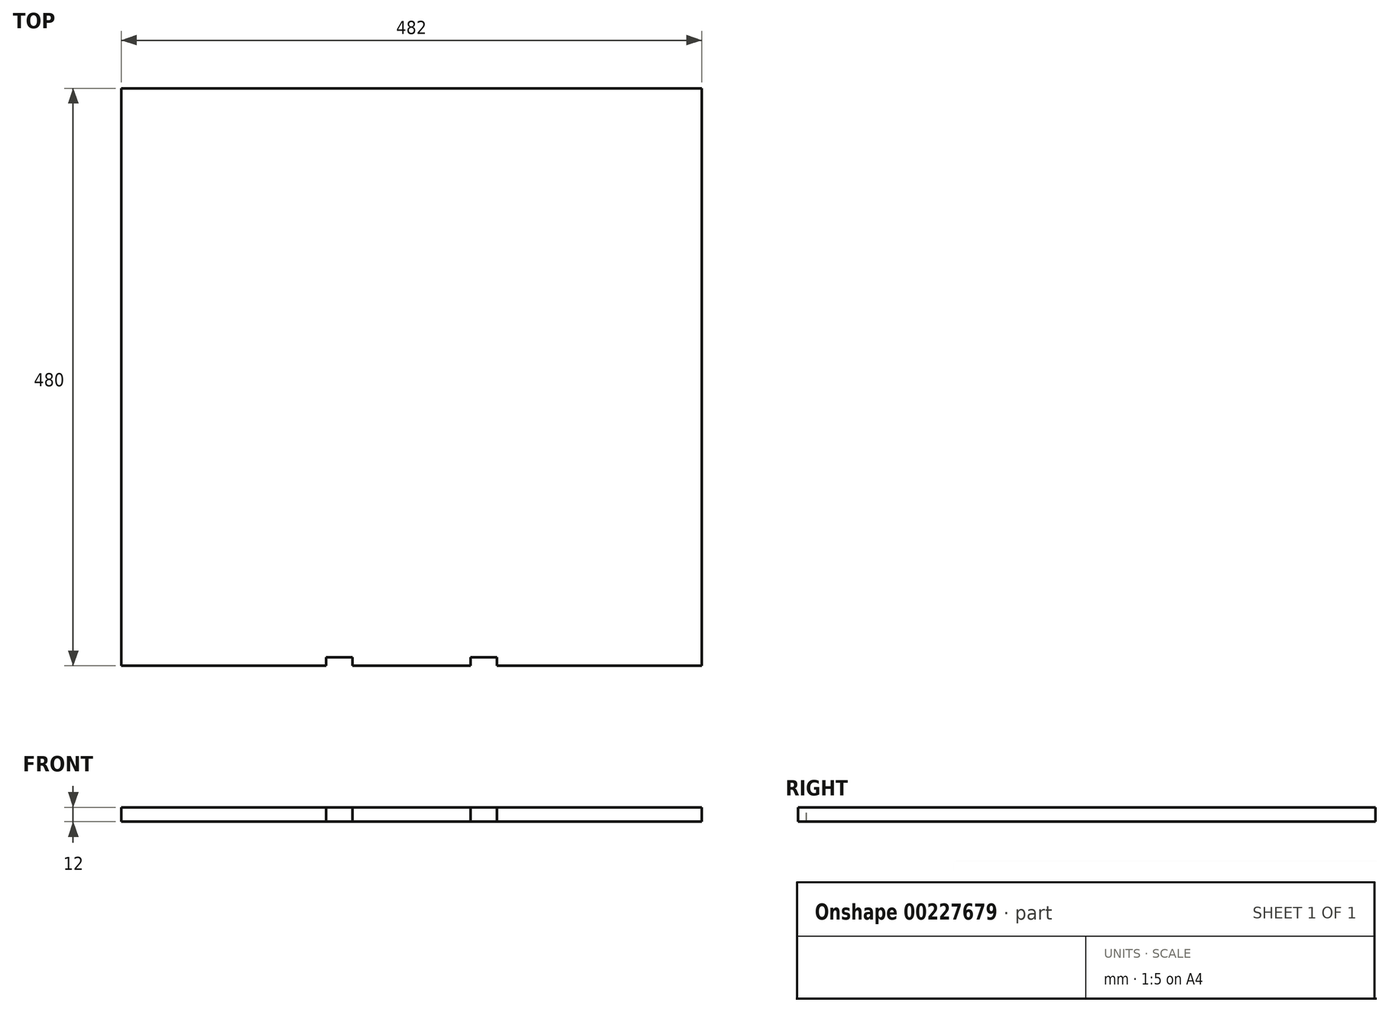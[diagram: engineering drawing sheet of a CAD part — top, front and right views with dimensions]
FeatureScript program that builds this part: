
annotation { "Feature Type Name" : "Feature", "Feature Type Description" : "" }
export const myFeature = defineFeature(function(context is Context, id is Id, definition is map)
    precondition{}
    {
        {
            var Q0;
            Q0=qCreatedBy(makeId("Top.planeOp"),FACE);
            var sketch = newSketch(context, id + "F0", { "sketchPlane" : qUnion([Q0])});
            skLineSegment(sketch, "E0.bottom", {"start": v(241, -240) * mm, "end": v(-241, -240) * mm});
            skLineSegment(sketch, "E0.top", {"start": v(241, 240) * mm, "end": v(-241, 240) * mm});
            skLineSegment(sketch, "E0.left", {"start": v(241, -240) * mm, "end": v(241, 240) * mm});
            skLineSegment(sketch, "E0.right", {"start": v(-241, -240) * mm, "end": v(-241, 240) * mm});
            skPoint(sketch, "E0.middle", {"position": v(0, 0) * mm});
            skSolve(sketch);
        }
        {
            var Q0;
            Q0=qSketchRegion(id+"F0",true);
            extrude(context, id + "F1", {"entities" : qUnion([Q0]), "depth" : 12 * mm, "symmetric" : true});
        }
        {
            var Q0;
            Q0=makeQuery(id+"F1.opExtrude","CAP_FACE",FACE,{"disambiguationData":[OSD([sQuery(id+"F0.wireOp",EDGE,"E0.bottom"),sQuery(id+"F0.wireOp",EDGE,"E0.top"),sQuery(id+"F0.wireOp",EDGE,"E0.left"),sQuery(id+"F0.wireOp",EDGE,"E0.right")])],"isStart":false});
            var sketch = newSketch(context, id + "F2", { "sketchPlane" : qUnion([Q0])});
            skLineSegment(sketch, "E1.bottom", {"start": v(-71, -240) * mm, "end": v(-49, -240) * mm});
            skLineSegment(sketch, "E1.top", {"start": v(-71, -233) * mm, "end": v(-49, -233) * mm});
            skLineSegment(sketch, "E1.left", {"start": v(-71, -240) * mm, "end": v(-71, -233) * mm});
            skLineSegment(sketch, "E1.right", {"start": v(-49, -240) * mm, "end": v(-49, -233) * mm});
            skPoint(sketch, "E2", {"position": v(-60, -240) * mm});
            skLineSegment(sketch, "E3", {"start": v(0, -240) * mm, "end": v(0, -197.24) * mm});
            skPoint(sketch, "E3.endSnap0", {"position": v(0, -240) * mm});
            skLineSegment(sketch, "E4.MirrorCS", {"start": v(71, -233) * mm, "end": v(49, -233) * mm});
            skLineSegment(sketch, "E5.MirrorCS", {"start": v(71, -240) * mm, "end": v(71, -233) * mm});
            skLineSegment(sketch, "E6.MirrorCS", {"start": v(49, -240) * mm, "end": v(49, -233) * mm});
            skLineSegment(sketch, "E7.MirrorCS", {"start": v(71, -240) * mm, "end": v(49, -240) * mm});
            skSolve(sketch);
        }
        {
            var Q0;
            Q0 = qSketchRegion(id + "F2", true);
            extrude(context, id + "F3", {"entities" : qUnion([Q0]), "operationType" : NewBodyOperationType.REMOVE, "endBound" : BoundingType.THROUGH_ALL, "oppositeDirection" : true, "depth" : 25 * mm});
        }
    });
